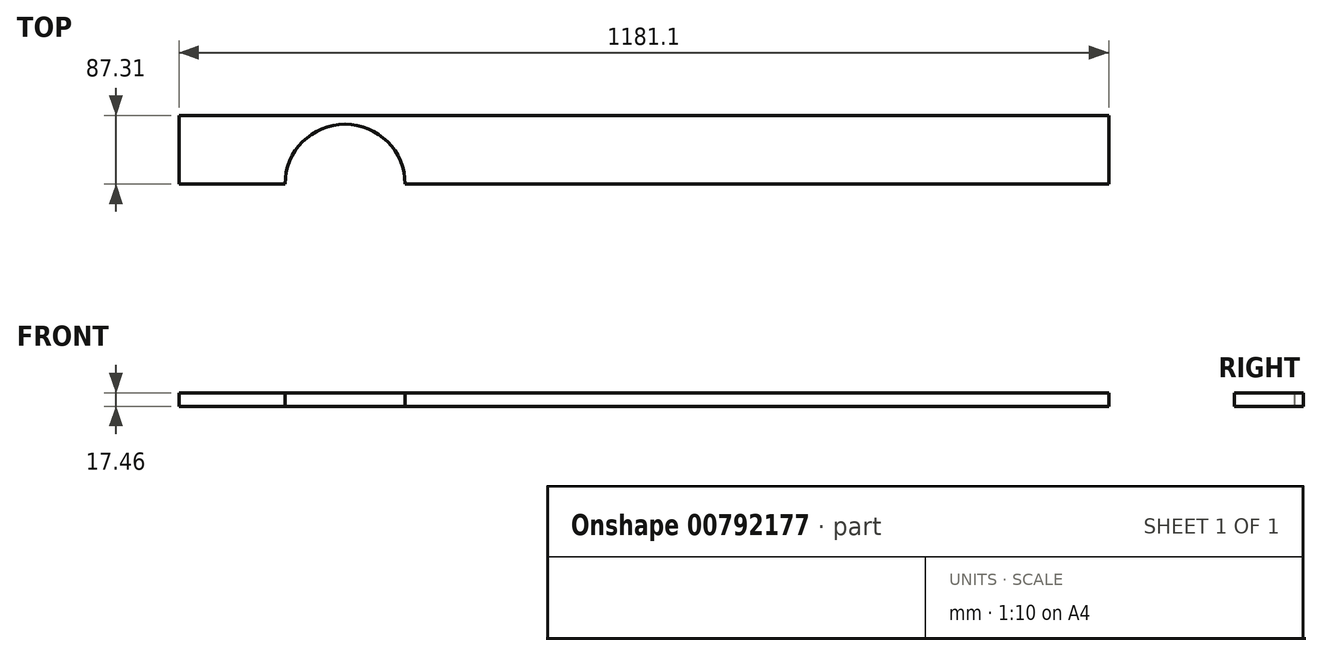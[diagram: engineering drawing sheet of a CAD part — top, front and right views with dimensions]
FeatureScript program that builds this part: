
annotation { "Feature Type Name" : "Feature", "Feature Type Description" : "" }
export const myFeature = defineFeature(function(context is Context, id is Id, definition is map)
    precondition{}
    {
        {
            var Q0;
            Q0=qCreatedBy(makeId("Top.planeOp"),FACE);
            var sketch = newSketch(context, id + "F0", { "sketchPlane" : qUnion([Q0])});
            skLineSegment(sketch, "E0.bottom", {"start": v(0, 0) * mm, "end": v(-893.76, 0) * mm});
            skLineSegment(sketch, "E0.top", {"start": v(0, 87.31) * mm, "end": v(-1181.1, 87.31) * mm});
            skLineSegment(sketch, "E0.left", {"start": v(0, 0) * mm, "end": v(0, 87.31) * mm});
            skLineSegment(sketch, "E0.right", {"start": v(-1181.1, 0) * mm, "end": v(-1181.1, 87.31) * mm});
            skArc(sketch, "E1", {"start": v(-893.76, 0) * mm, "mid": v(-969.96, 76.2) * mm, "end": v(-1046.16, 0) * mm});
            skLineSegment(sketch, "E2.trimOffspring", {"start": v(-1046.16, 0) * mm, "end": v(-1181.1, 0) * mm});
            skSolve(sketch);
        }
        {
            var Q0;
            Q0 = qSketchRegion(id + "F0", true);
            extrude(context, id + "F1", {"entities" : qUnion([Q0]), "depth" : 17.46 * mm, "offsetDistance" : 25.4 * mm});
        }
    });
